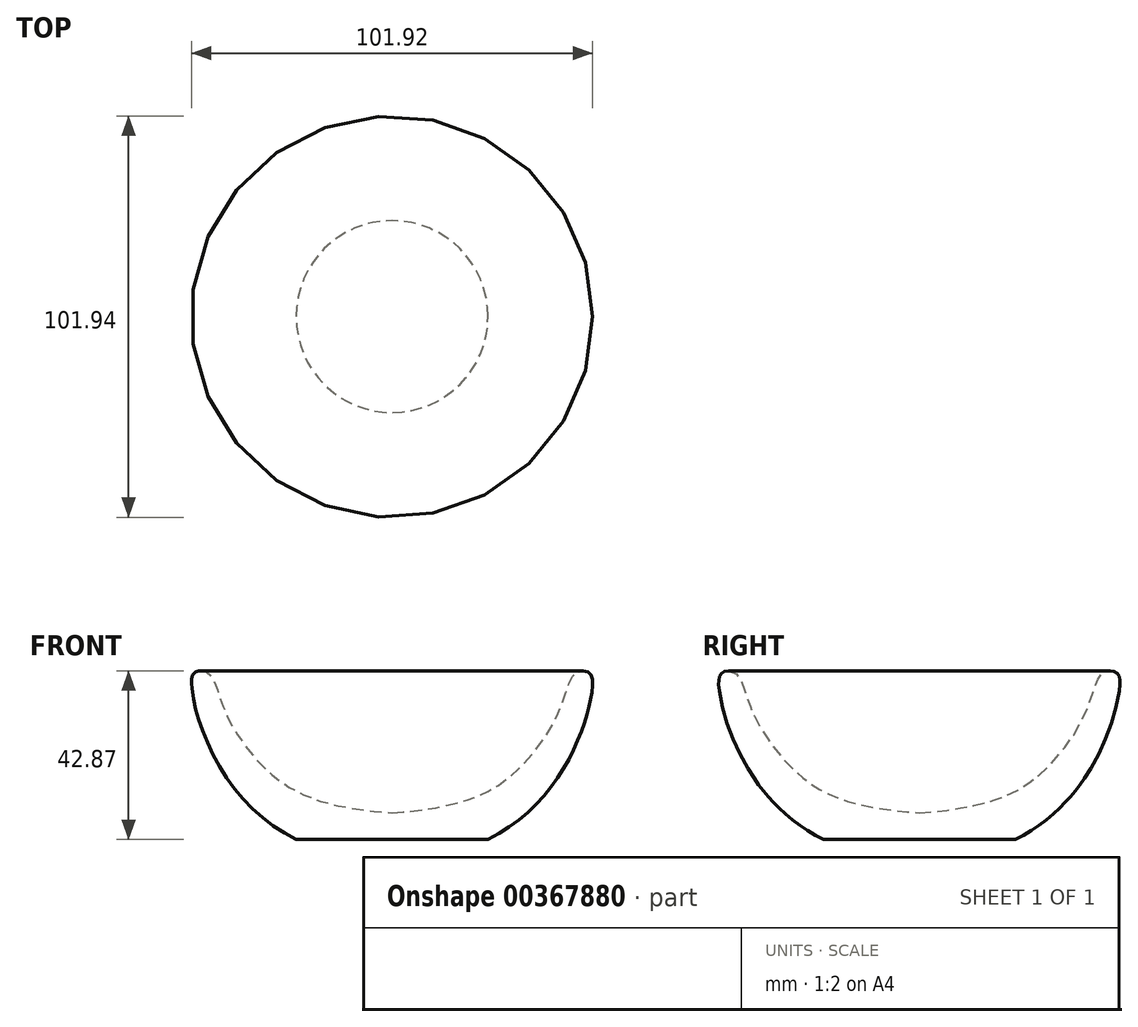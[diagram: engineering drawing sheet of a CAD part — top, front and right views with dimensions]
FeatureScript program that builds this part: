
annotation { "Feature Type Name" : "Feature", "Feature Type Description" : "" }
export const myFeature = defineFeature(function(context is Context, id is Id, definition is map)
    precondition{}
    {
        {
            var Q0;
            Q0=qCreatedBy(makeId("Front.planeOp"),FACE);
            var sketch = newSketch(context, id + "F0", { "sketchPlane" : qUnion([Q0])});
            skLineSegment(sketch, "E0", {"start": v(0, 6.75) * mm, "end": v(0, 0) * mm});
            skLineSegment(sketch, "E1", {"start": v(0, 0) * mm, "end": v(24.38, 0) * mm});
            skFitSpline(sketch, "E2", {"points": [v(0, 6.75) * mm, v(14.68, 8.81) * mm, v(29.08, 15.27) * mm, v(42.59, 32.9) * mm, v(46.7, 42.3) * mm, v(50.22, 42.3) * mm, v(50.8, 37.89) * mm, v(48.46, 28.49) * mm, v(40.53, 13.5) * mm, v(24.38, 0) * mm], "startDerivative": vector(123.06, 9.2) * mm, "endDerivative": vector(-139.75, -70.76) * mm});
            skPoint(sketch, "E3.orphan", {"position": v(0, 29.66) * mm});
            skSolve(sketch);
        }
        {
            var Q0;
            Q0=makeQuery(id+"F0.imprint","IMPRINT",FACE,{"disambiguationData":[TD([[makeQuery(id+"F0.imprint","IMPRINT",EDGE,{"derivedFrom":sQuery(id+"F0.wireOp",EDGE,"E0")}),1.0]])]});
            var Q1;
            Q1=sQuery(id+"F0.wireOp",EDGE,"E0");
            revolve(context, id + "F1", {"entities" : qUnion([Q0]), "axis" : qUnion([Q1]), "revolveType" : RevolveType.FULL});
        }
    });
